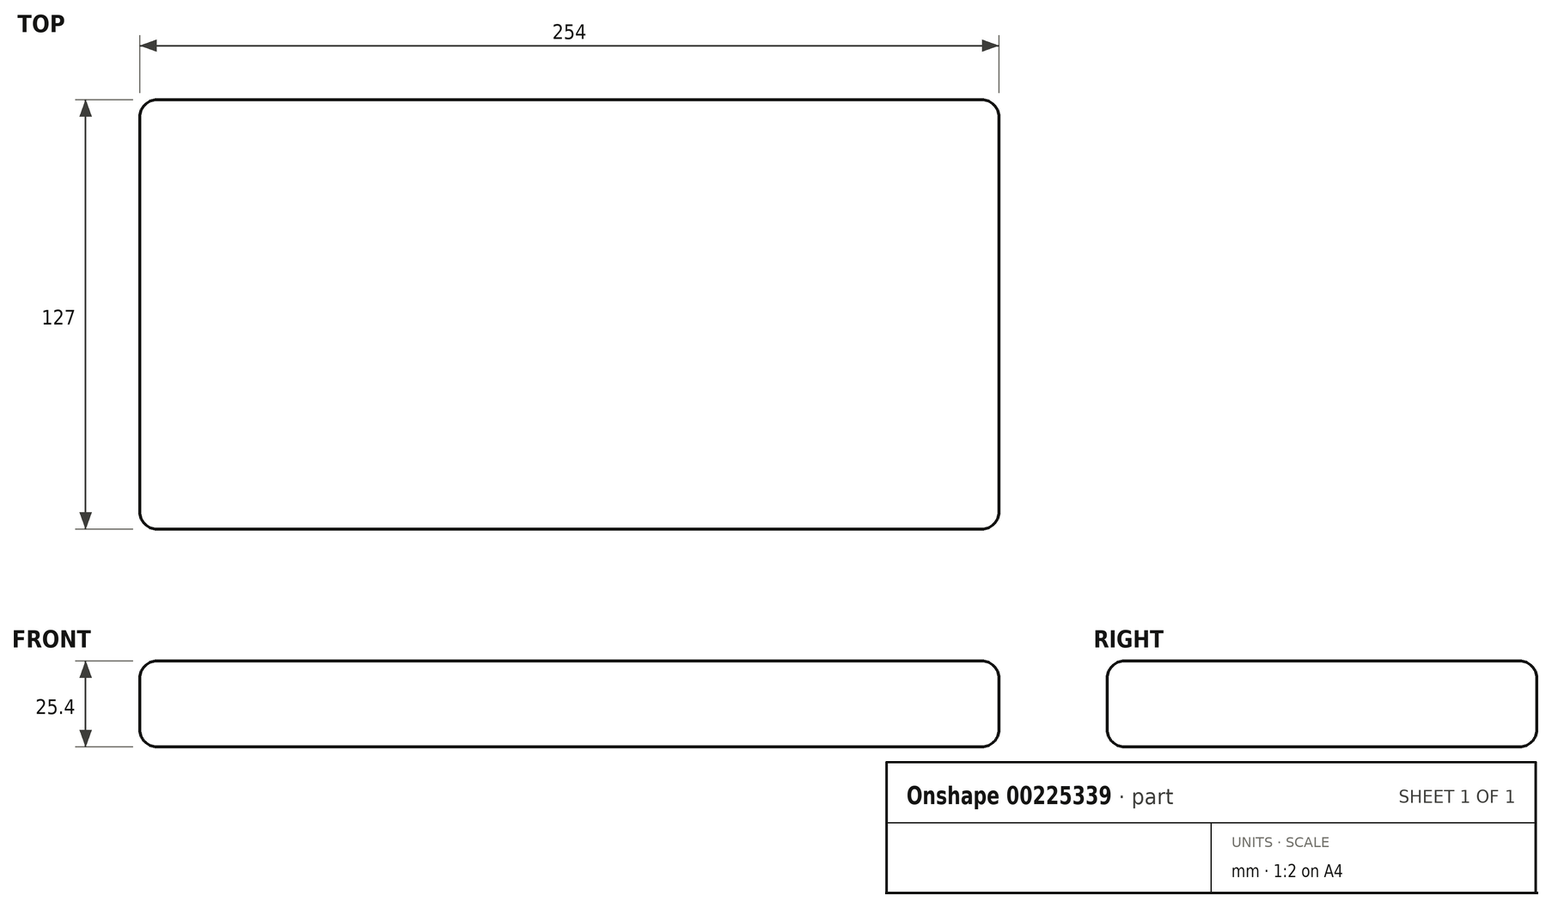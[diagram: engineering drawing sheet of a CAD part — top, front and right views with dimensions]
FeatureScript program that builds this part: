
annotation { "Feature Type Name" : "Feature", "Feature Type Description" : "" }
export const myFeature = defineFeature(function(context is Context, id is Id, definition is map)
    precondition{}
    {
        {
            var Q0;
            Q0=qCreatedBy(makeId("Top.planeOp"),FACE);
            var sketch = newSketch(context, id + "F0", { "sketchPlane" : qUnion([Q0])});
            skLineSegment(sketch, "E0.bottom", {"start": v(127, 63.5) * mm, "end": v(-127, 63.5) * mm});
            skLineSegment(sketch, "E0.top", {"start": v(127, -63.5) * mm, "end": v(-127, -63.5) * mm});
            skLineSegment(sketch, "E0.left", {"start": v(127, 63.5) * mm, "end": v(127, -63.5) * mm});
            skLineSegment(sketch, "E0.right", {"start": v(-127, 63.5) * mm, "end": v(-127, -63.5) * mm});
            skPoint(sketch, "E0.middle", {"position": v(0, 0) * mm});
            skSolve(sketch);
        }
        {
            var Q0;
            Q0 = qSketchRegion(id + "F0", true);
            extrude(context, id + "F1", {"entities" : qUnion([Q0]), "depth" : 25.4 * mm});
        }
        {
            var Q0;
            Q0=makeQuery(id+"F1.opExtrude","SWEPT_FACE",FACE,{"disambiguationData":[OSD([sQuery(id+"F0.wireOp",EDGE,"E0.bottom")])]});
            var Q1;
            Q1=makeQuery(id+"F1.opExtrude","SWEPT_FACE",FACE,{"disambiguationData":[OSD([sQuery(id+"F0.wireOp",EDGE,"E0.left")])]});
            var Q2;
            Q2=makeQuery(id+"F1.opExtrude","SWEPT_FACE",FACE,{"disambiguationData":[OSD([sQuery(id+"F0.wireOp",EDGE,"E0.top")])]});
            var Q3;
            Q3=makeQuery(id+"F1.opExtrude","CAP_FACE",FACE,{"disambiguationData":[OSD([sQuery(id+"F0.wireOp",EDGE,"E0.bottom"),sQuery(id+"F0.wireOp",EDGE,"E0.top"),sQuery(id+"F0.wireOp",EDGE,"E0.left"),sQuery(id+"F0.wireOp",EDGE,"E0.right")])],"isStart":false});
            var Q4;
            Q4=makeQuery(id+"F1.opExtrude","CAP_FACE",FACE,{"disambiguationData":[OSD([sQuery(id+"F0.wireOp",EDGE,"E0.bottom"),sQuery(id+"F0.wireOp",EDGE,"E0.top"),sQuery(id+"F0.wireOp",EDGE,"E0.left"),sQuery(id+"F0.wireOp",EDGE,"E0.right")])],"isStart":true});
            fillet(context, id + "F2", {"entities" : qUnion([Q0, Q1, Q2, Q3, Q4]), "radius" : 5.08 * mm, "tangentPropagation" : true, "allowEdgeOverflow" : false});
        }
    });
